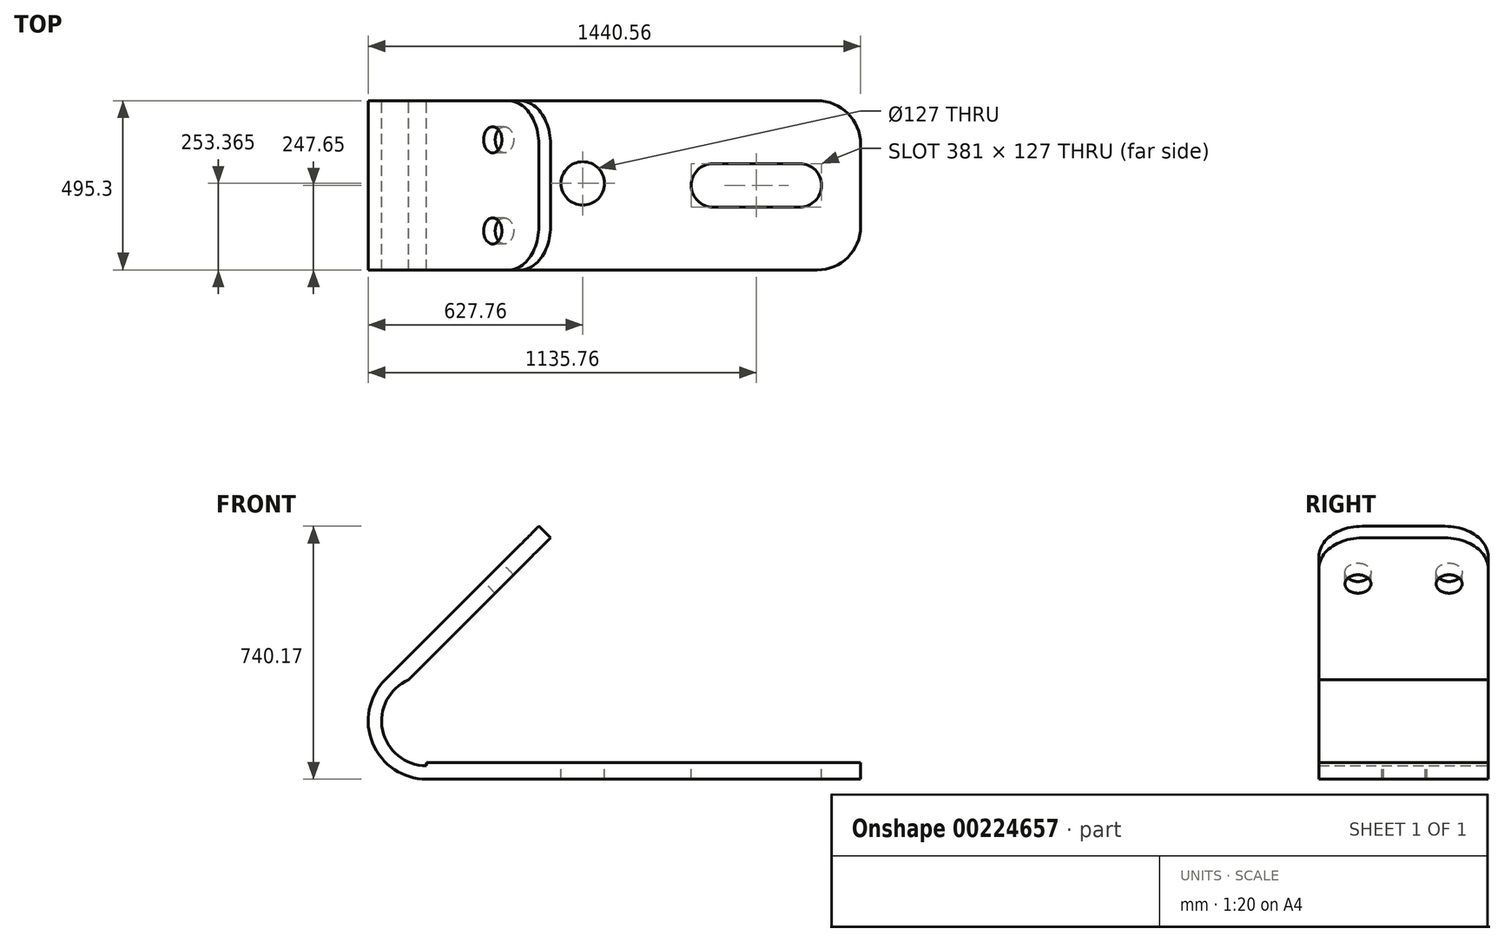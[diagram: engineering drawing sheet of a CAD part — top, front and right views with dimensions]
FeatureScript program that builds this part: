
annotation { "Feature Type Name" : "Feature", "Feature Type Description" : "" }
export const myFeature = defineFeature(function(context is Context, id is Id, definition is map)
    precondition{}
    {
        {
            var Q0;
            Q0=qCreatedBy(makeId("Front.planeOp"),FACE);
            var sketch = newSketch(context, id + "F0", { "sketchPlane" : qUnion([Q0])});
            skLineSegment(sketch, "E0.bottom", {"start": v(635, 24.13) * mm, "end": v(-635, 24.13) * mm});
            skLineSegment(sketch, "E0.top", {"start": v(635, -24.13) * mm, "end": v(-635, -24.13) * mm});
            skLineSegment(sketch, "E0.left", {"start": v(635, 24.13) * mm, "end": v(635, -24.13) * mm});
            skLineSegment(sketch, "E0.right", {"start": v(-635, 24.13) * mm, "end": v(-635, -24.13) * mm});
            skPoint(sketch, "E0.middle", {"position": v(0, 0) * mm});
            skArc(sketch, "E1", {"start": v(-635, -24.13) * mm, "mid": v(-792.57, 81.16) * mm, "end": v(-755.6, 267.03) * mm});
            skLineSegment(sketch, "E2", {"start": v(-755.6, 267.03) * mm, "end": v(-306.59, 716.04) * mm});
            skLineSegment(sketch, "E3", {"start": v(-306.59, 716.04) * mm, "end": v(-272.46, 681.91) * mm});
            skLineSegment(sketch, "E4", {"start": v(-272.46, 681.91) * mm, "end": v(-687.35, 267.03) * mm});
            skArc(sketch, "E5", {"start": v(-687.35, 267.03) * mm, "mid": v(-763.73, 119.7) * mm, "end": v(-635, 14.95) * mm});
            skSolve(sketch);
        }
        {
            var Q0;
            Q0 = qSketchRegion(id + "F0", true);
            extrude(context, id + "F1", {"entities" : qUnion([Q0]), "depth" : 495.3 * mm});
        }
        {
            var Q0;
            Q0=makeQuery(id+"F1.opExtrude","SWEPT_FACE",FACE,{"disambiguationData":[OSD([sQuery(id+"F0.wireOp",EDGE,"E2")])]});
            var sketch = newSketch(context, id + "F2", { "sketchPlane" : qUnion([Q0])});
            skLineSegment(sketch, "E6", {"start": v(0, 289.53) * mm, "end": v(114.3, 289.53) * mm});
            skLineSegment(sketch, "E7", {"start": v(495.3, 289.53) * mm, "end": v(381, 289.53) * mm});
            skLineSegment(sketch, "E8", {"start": v(114.3, 289.53) * mm, "end": v(114.3, 99.03) * mm});
            skLineSegment(sketch, "E9", {"start": v(381, 289.53) * mm, "end": v(381, 99.03) * mm});
            skCircle(sketch, "E10", {"center": v(114.3, 99.03) * mm, "radius": 38.1 * mm});
            skCircle(sketch, "E11", {"center": v(381, 99.03) * mm, "radius": 38.1 * mm});
            skSolve(sketch);
        }
        {
            var Q0;
            Q0=makeQuery(id+"F2.imprint","IMPRINT",FACE,{"disambiguationData":[TD([[makeQuery(id+"F2.imprint","IMPRINT",EDGE,{"derivedFrom":sQuery(id+"F2.wireOp",EDGE,"E10")}),1.0]])]});
            var Q1;
            Q1=makeQuery(id+"F2.imprint","IMPRINT",FACE,{"disambiguationData":[TD([[makeQuery(id+"F2.imprint","IMPRINT",EDGE,{"derivedFrom":sQuery(id+"F2.wireOp",EDGE,"E11")}),1.0]])]});
            extrude(context, id + "F3", {"entities" : qUnion([Q0, Q1]), "operationType" : NewBodyOperationType.REMOVE, "oppositeDirection" : true, "depth" : 101.6 * mm});
        }
        {
            var Q0;
            Q0=makeQuery(id+"F1.opExtrude","SWEPT_FACE",FACE,{"disambiguationData":[OSD([sQuery(id+"F0.wireOp",EDGE,"E0.bottom")])]});
            var sketch = newSketch(context, id + "F4", { "sketchPlane" : qUnion([Q0])});
            skLineSegment(sketch, "E12", {"start": v(635, 0) * mm, "end": v(-177.8, 0) * mm});
            skCircle(sketch, "E13", {"center": v(-177.8, -241.94) * mm, "radius": 63.5 * mm});
            skLineSegment(sketch, "E14", {"start": v(635, -247.65) * mm, "end": v(520.7, -247.65) * mm});
            skArc(sketch, "E15", {"start": v(520.7, -247.65) * mm, "mid": v(502.1, -292.55) * mm, "end": v(457.2, -311.15) * mm});
            skArc(sketch, "E16", {"start": v(520.7, -247.65) * mm, "mid": v(502.1, -202.75) * mm, "end": v(457.2, -184.15) * mm});
            skLineSegment(sketch, "E17", {"start": v(520.7, -247.65) * mm, "end": v(139.7, -247.65) * mm});
            skArc(sketch, "E18", {"start": v(139.7, -247.65) * mm, "mid": v(158.3, -292.55) * mm, "end": v(203.2, -311.15) * mm});
            skArc(sketch, "E19", {"start": v(139.7, -247.65) * mm, "mid": v(158.3, -202.75) * mm, "end": v(203.2, -184.15) * mm});
            skLineSegment(sketch, "E20", {"start": v(457.2, -184.15) * mm, "end": v(203.2, -184.15) * mm});
            skLineSegment(sketch, "E21", {"start": v(457.2, -311.15) * mm, "end": v(203.2, -311.15) * mm});
            skSolve(sketch);
        }
        {
            var Q0;
            Q0 = qSketchRegion(id + "F4", true);
            extrude(context, id + "F5", {"entities" : qUnion([Q0]), "operationType" : NewBodyOperationType.REMOVE, "oppositeDirection" : true, "depth" : 101.6 * mm});
        }
        {
            var Q0;
            Q0=makeQuery(id+"F1.opExtrude","SWEPT_FACE",FACE,{"disambiguationData":[OSD([sQuery(id+"F0.wireOp",EDGE,"E2")])]});
            var sketch = newSketch(context, id + "F6", { "sketchPlane" : qUnion([Q0])});
            skLineSegment(sketch, "E22", {"start": v(0, 289.53) * mm, "end": v(254, 289.53) * mm});
            skLineSegment(sketch, "E23", {"start": v(254, 289.53) * mm, "end": v(254, 35.53) * mm});
            skLineSegment(sketch, "E24", {"start": v(254, 35.53) * mm, "end": v(0, 35.53) * mm});
            skLineSegment(sketch, "E25", {"start": v(0, 35.53) * mm, "end": v(0, 289.53) * mm});
            skLineSegment(sketch, "E26", {"start": v(127, 289.53) * mm, "end": v(127, 162.53) * mm});
            skPoint(sketch, "E26.endSnap0", {"position": v(127, 35.53) * mm});
            skCircle(sketch, "E27", {"center": v(127, 162.53) * mm, "radius": 127 * mm});
            skLineSegment(sketch, "E28", {"start": v(0, 162.53) * mm, "end": v(254, 162.53) * mm});
            skSolve(sketch);
        }
        {
            var Q0;
            {var subQ0=sQuery(id+"F6.wireOp",EDGE,"E25");var subQ1=sQuery(id+"F6.wireOp",EDGE,"E22");var subQ2=makeQuery(id+"F6.imprint","INTERSECT",VERTEX,{"derivedFrom":[subQ1,subQ0]});Q0=makeQuery(id+"F6.imprint","IMPRINT",FACE,{"disambiguationData":[TD([[makeQuery(id+"F6.imprint","IMPRINT",EDGE,{"disambiguationData":[TD([[subQ2,1.0]])],"derivedFrom":subQ1}),1.0]])]});}
            extrude(context, id + "F7", {"entities" : qUnion([Q0]), "operationType" : NewBodyOperationType.REMOVE, "oppositeDirection" : true, "depth" : 127 * mm});
        }
        {
            var Q0;
            Q0=makeQuery(id+"F1.opExtrude","SWEPT_FACE",FACE,{"disambiguationData":[OSD([sQuery(id+"F0.wireOp",EDGE,"E2")])]});
            var sketch = newSketch(context, id + "F8", { "sketchPlane" : qUnion([Q0])});
            skLineSegment(sketch, "E29.bottom", {"start": v(495.3, 289.53) * mm, "end": v(241.3, 289.53) * mm});
            skLineSegment(sketch, "E29.top", {"start": v(495.3, 35.53) * mm, "end": v(241.3, 35.53) * mm});
            skLineSegment(sketch, "E29.left", {"start": v(495.3, 289.53) * mm, "end": v(495.3, 35.53) * mm});
            skLineSegment(sketch, "E29.right", {"start": v(241.3, 289.53) * mm, "end": v(241.3, 35.53) * mm});
            skLineSegment(sketch, "E30", {"start": v(368.3, 289.53) * mm, "end": v(368.3, 162.53) * mm});
            skCircle(sketch, "E31", {"center": v(368.3, 162.53) * mm, "radius": 127 * mm});
            skSolve(sketch);
        }
        {
            var Q0;
            {var subQ0=sQuery(id+"F8.wireOp",EDGE,"E29.left");var subQ1=sQuery(id+"F8.wireOp",EDGE,"E29.bottom");var subQ2=makeQuery(id+"F8.imprint","INTERSECT",VERTEX,{"derivedFrom":[subQ1,subQ0]});Q0=makeQuery(id+"F8.imprint","IMPRINT",FACE,{"disambiguationData":[TD([[makeQuery(id+"F8.imprint","IMPRINT",EDGE,{"disambiguationData":[TD([[subQ2,-1.0]])],"derivedFrom":subQ1}),1.0]])]});}
            extrude(context, id + "F9", {"entities" : qUnion([Q0]), "operationType" : NewBodyOperationType.REMOVE, "oppositeDirection" : true, "depth" : 127 * mm});
        }
        {
            var Q0;
            Q0=makeQuery(id+"F1.opExtrude","SWEPT_FACE",FACE,{"disambiguationData":[OSD([sQuery(id+"F0.wireOp",EDGE,"E0.top")])]});
            var sketch = newSketch(context, id + "F10", { "sketchPlane" : qUnion([Q0])});
            skLineSegment(sketch, "E32.bottom", {"start": v(635, 495.3) * mm, "end": v(381, 495.3) * mm});
            skLineSegment(sketch, "E32.top", {"start": v(635, 241.3) * mm, "end": v(381, 241.3) * mm});
            skLineSegment(sketch, "E32.left", {"start": v(635, 495.3) * mm, "end": v(635, 241.3) * mm});
            skLineSegment(sketch, "E32.right", {"start": v(381, 495.3) * mm, "end": v(381, 241.3) * mm});
            skLineSegment(sketch, "E33", {"start": v(635, 368.3) * mm, "end": v(508, 368.3) * mm});
            skCircle(sketch, "E34", {"center": v(508, 368.3) * mm, "radius": 127 * mm});
            skSolve(sketch);
        }
        {
            var Q0;
            {var subQ0=sQuery(id+"F10.wireOp",EDGE,"E32.left");var subQ1=sQuery(id+"F10.wireOp",EDGE,"E32.bottom");var subQ2=makeQuery(id+"F10.imprint","INTERSECT",VERTEX,{"derivedFrom":[subQ1,subQ0]});Q0=makeQuery(id+"F10.imprint","IMPRINT",FACE,{"disambiguationData":[TD([[makeQuery(id+"F10.imprint","IMPRINT",EDGE,{"disambiguationData":[TD([[subQ2,-1.0]])],"derivedFrom":subQ1}),1.0]])]});}
            extrude(context, id + "F11", {"entities" : qUnion([Q0]), "operationType" : NewBodyOperationType.REMOVE, "oppositeDirection" : true, "depth" : 127 * mm});
        }
        {
            var Q0;
            Q0=makeQuery(id+"F1.opExtrude","SWEPT_FACE",FACE,{"disambiguationData":[OSD([sQuery(id+"F0.wireOp",EDGE,"E0.top")])]});
            var sketch = newSketch(context, id + "F12", { "sketchPlane" : qUnion([Q0])});
            skLineSegment(sketch, "E35.bottom", {"start": v(635, 0) * mm, "end": v(381, 0) * mm});
            skLineSegment(sketch, "E35.top", {"start": v(635, 254) * mm, "end": v(381, 254) * mm});
            skLineSegment(sketch, "E35.left", {"start": v(635, 0) * mm, "end": v(635, 254) * mm});
            skLineSegment(sketch, "E35.right", {"start": v(381, 0) * mm, "end": v(381, 254) * mm});
            skLineSegment(sketch, "E36", {"start": v(635, 127) * mm, "end": v(508, 127) * mm});
            skCircle(sketch, "E37", {"center": v(508, 127) * mm, "radius": 127 * mm});
            skSolve(sketch);
        }
        {
            var Q0;
            {var subQ0=sQuery(id+"F12.wireOp",EDGE,"E35.left");var subQ1=sQuery(id+"F12.wireOp",EDGE,"E35.bottom");var subQ2=makeQuery(id+"F12.imprint","INTERSECT",VERTEX,{"derivedFrom":[subQ1,subQ0]});Q0=makeQuery(id+"F12.imprint","IMPRINT",FACE,{"disambiguationData":[TD([[makeQuery(id+"F12.imprint","IMPRINT",EDGE,{"disambiguationData":[TD([[subQ2,-1.0]])],"derivedFrom":subQ1}),-1.0]])]});}
            extrude(context, id + "F13", {"entities" : qUnion([Q0]), "operationType" : NewBodyOperationType.REMOVE, "oppositeDirection" : true, "depth" : 127 * mm});
        }
    });
